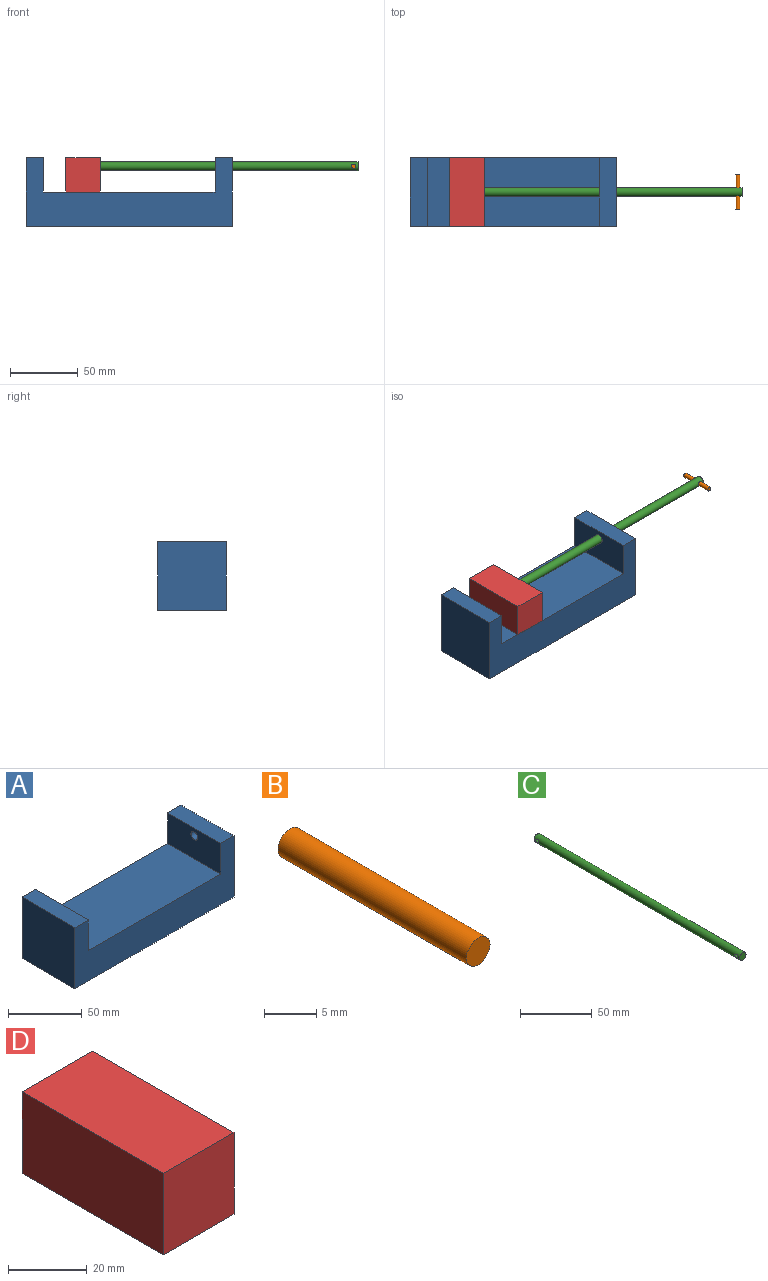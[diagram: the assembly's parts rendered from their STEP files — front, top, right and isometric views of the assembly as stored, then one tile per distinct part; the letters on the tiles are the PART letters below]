
ASSEMBLY  parts=4 mates=3
PART A: 11 faces, bbox 152.4x50.8x50.8 mm
  f0: plane 127x50.8mm, normal (0,0,1), area 6451.6mm2, adj f2,f4,f6,f8
  f1: plane 50.8x50.8mm, normal (1,0,0), area 2549mm2, adj f2,f4,f5,f9,f10
  f2: plane 152.4x50.8mm, normal (0,1,0), area 4516.1mm2, adj f0,f1,f3,f5,f6,f7,f8,f9
  f3: plane 50.8x50.8mm, normal (-1,0,0), area 2580.6mm2, adj f2,f4,f5,f7
  f4: plane 152.4x50.8mm, normal (0,-1,0), area 4516.1mm2, adj f0,f1,f3,f5,f6,f7,f8,f9
  f5: plane 152.4x50.8mm, normal (0,0,-1), area 7741.9mm2, adj f1,f2,f3,f4
  f6: plane 50.8x25.4mm, normal (1,0,0), area 1290.3mm2, adj f0,f2,f4,f7
  f7: plane 50.8x12.7mm, normal (0,0,1), area 645.2mm2, adj f2,f3,f4,f6
  f8: plane 50.8x25.4mm, normal (-1,0,0), area 1258.7mm2, adj f0,f2,f4,f9,f10
  f9: plane 50.8x12.7mm, normal (0,0,1), area 645.2mm2, adj f1,f2,f4,f8
  f10: cylinder r=3.17mm len=12.7mm, axis (1,0,0), area 253.4mm2, adj f1,f8
PART B: 3 faces, bbox 3.2x25.4x3.2 mm
  f0: cylinder r=1.59mm len=25.4mm, axis (0,1,0), area 253.4mm2, adj f1,f2
  f1: plane 3.18x3.18mm, normal (0,-1,0), area 7.9mm2, adj f0
  f2: plane 3.18x3.18mm, normal (0,1,0), area 7.9mm2, adj f0
PART C: 5 faces, bbox 6.4x203.2x6.4 mm
  f0: cylinder r=3.17mm len=203.2mm, axis (0,1,0), area 4021mm2, adj f1,f2,f3,f4
  f1: plane 6.35x6.35mm, normal (0,-1,0), area 31.7mm2, adj f0
  f2: plane 6.35x6.35mm, normal (0,1,0), area 31.7mm2, adj f0
  f3: cylinder r=1.59mm len=6.35mm, axis (1,0,0), area 59.2mm2, adj f0
  f4: cylinder r=1.59mm len=6.35mm, axis (1,0,0), area 59.2mm2, adj f0
PART D: 8 faces, bbox 25.4x50.8x25.4 mm
  f0: plane 25.4x25.4mm, normal (0,-1,0), area 645.2mm2, adj f1,f3,f4,f5
  f1: plane 50.8x25.4mm, normal (1,0,0), area 1258.7mm2, adj f0,f2,f4,f5,f6
  f2: plane 25.4x25.4mm, normal (0,1,0), area 645.2mm2, adj f1,f3,f4,f5
  f3: plane 50.8x25.4mm, normal (-1,0,0), area 1290.3mm2, adj f0,f2,f4,f5
  f4: plane 50.8x25.4mm, normal (0,0,1), area 1290.3mm2, adj f0,f1,f2,f3
  f5: plane 50.8x25.4mm, normal (0,0,-1), area 1290.3mm2, adj f0,f1,f2,f3
  f6: cylinder r=3.17mm len=12.7mm, axis (1,0,0), area 253.4mm2, adj f1,f7
  f7: cone r=0mm half-angle=59deg, axis (1,0,0), area 36.9mm2, adj f6
PLACE A t=(-22.58,0.12,-5.66)mm fixed
PLACE B t=(143.43,0.12,38.79)mm
PLACE C rot(axis=(0.71,0.71,0),180deg) t=(45.01,0.12,38.79)mm
PLACE D rot(axis=(-1,0,0),0deg) t=(-56.59,0.12,19.74)mm
MATE cylindrical D.f6 <-> C.f0  axis (1,0,0) through (-56.59,0.12,38.79)mm
MATE slider A.f6 <-> D.f3  axis (-1,0,0) through (-86.08,-25.28,19.74)mm
MATE cylindrical B.f0 <-> C.f4  axis (0,1,0) through (143.43,0.12,38.79)mm
